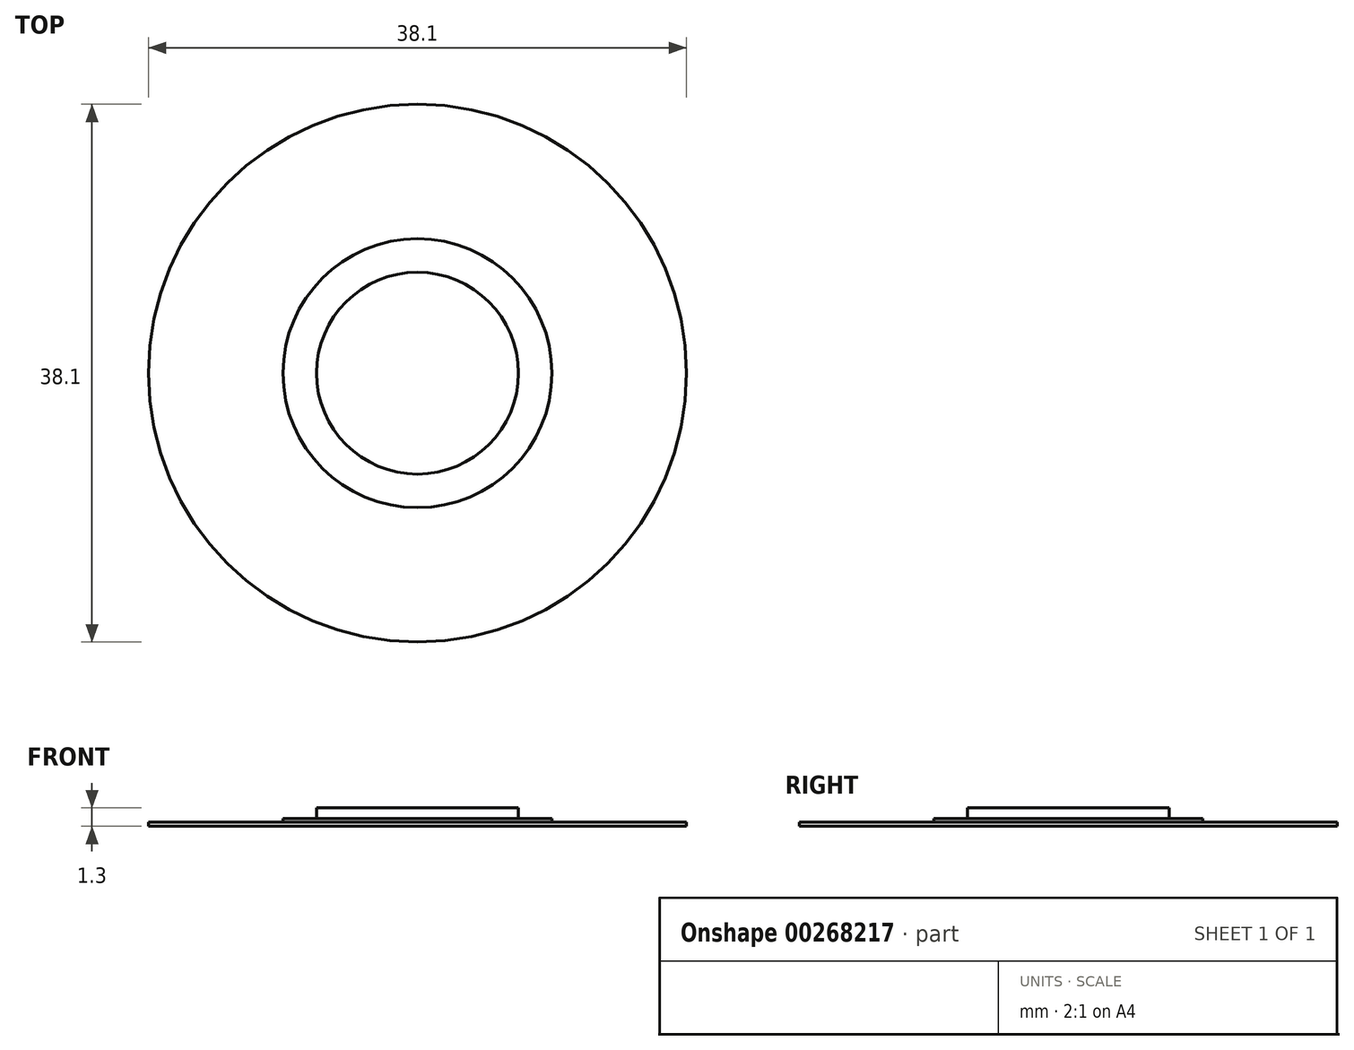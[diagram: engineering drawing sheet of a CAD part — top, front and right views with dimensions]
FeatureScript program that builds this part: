
annotation { "Feature Type Name" : "Feature", "Feature Type Description" : "" }
export const myFeature = defineFeature(function(context is Context, id is Id, definition is map)
    precondition{}
    {
        {
            var Q0;
            Q0=qCreatedBy(makeId("Top.planeOp"),FACE);
            var sketch = newSketch(context, id + "F0", { "sketchPlane" : qUnion([Q0])});
            skCircle(sketch, "E0", {"center": v(0, 0) * mm, "radius": 22.86 * mm});
            skCircle(sketch, "E1", {"center": v(0, 0) * mm, "radius": 9.53 * mm});
            skCircle(sketch, "E2", {"center": v(0, 0) * mm, "radius": 7.15 * mm});
            skCircle(sketch, "E3", {"center": v(0, 0) * mm, "radius": 19.05 * mm});
            skSolve(sketch);
        }
        {
            var Q0;
            Q0=makeQuery(id+"F0.imprint","IMPRINT",FACE,{"disambiguationData":[TD([[makeQuery(id+"F0.imprint","IMPRINT",EDGE,{"derivedFrom":sQuery(id+"F0.wireOp",EDGE,"E1")}),-1.0]])]});
            extrude(context, id + "F1", {"entities" : qUnion([Q0]), "depth" : 0.3 * mm});
        }
        {
            var Q0;
            Q0=makeQuery(id+"F0.imprint","IMPRINT",FACE,{"disambiguationData":[TD([[makeQuery(id+"F0.imprint","IMPRINT",EDGE,{"derivedFrom":sQuery(id+"F0.wireOp",EDGE,"E1")}),1.0]])]});
            extrude(context, id + "F2", {"entities" : qUnion([Q0]), "operationType" : NewBodyOperationType.ADD, "depth" : .25 * mm + 0.3 * mm});
        }
        {
            var Q0;
            Q0=makeQuery(id+"F0.imprint","IMPRINT",FACE,{"disambiguationData":[TD([[makeQuery(id+"F0.imprint","IMPRINT",EDGE,{"derivedFrom":sQuery(id+"F0.wireOp",EDGE,"E2")}),1.0]])]});
            extrude(context, id + "F3", {"entities" : qUnion([Q0]), "operationType" : NewBodyOperationType.ADD, "depth" : 1 * mm + 0.3 * mm});
        }
    });
